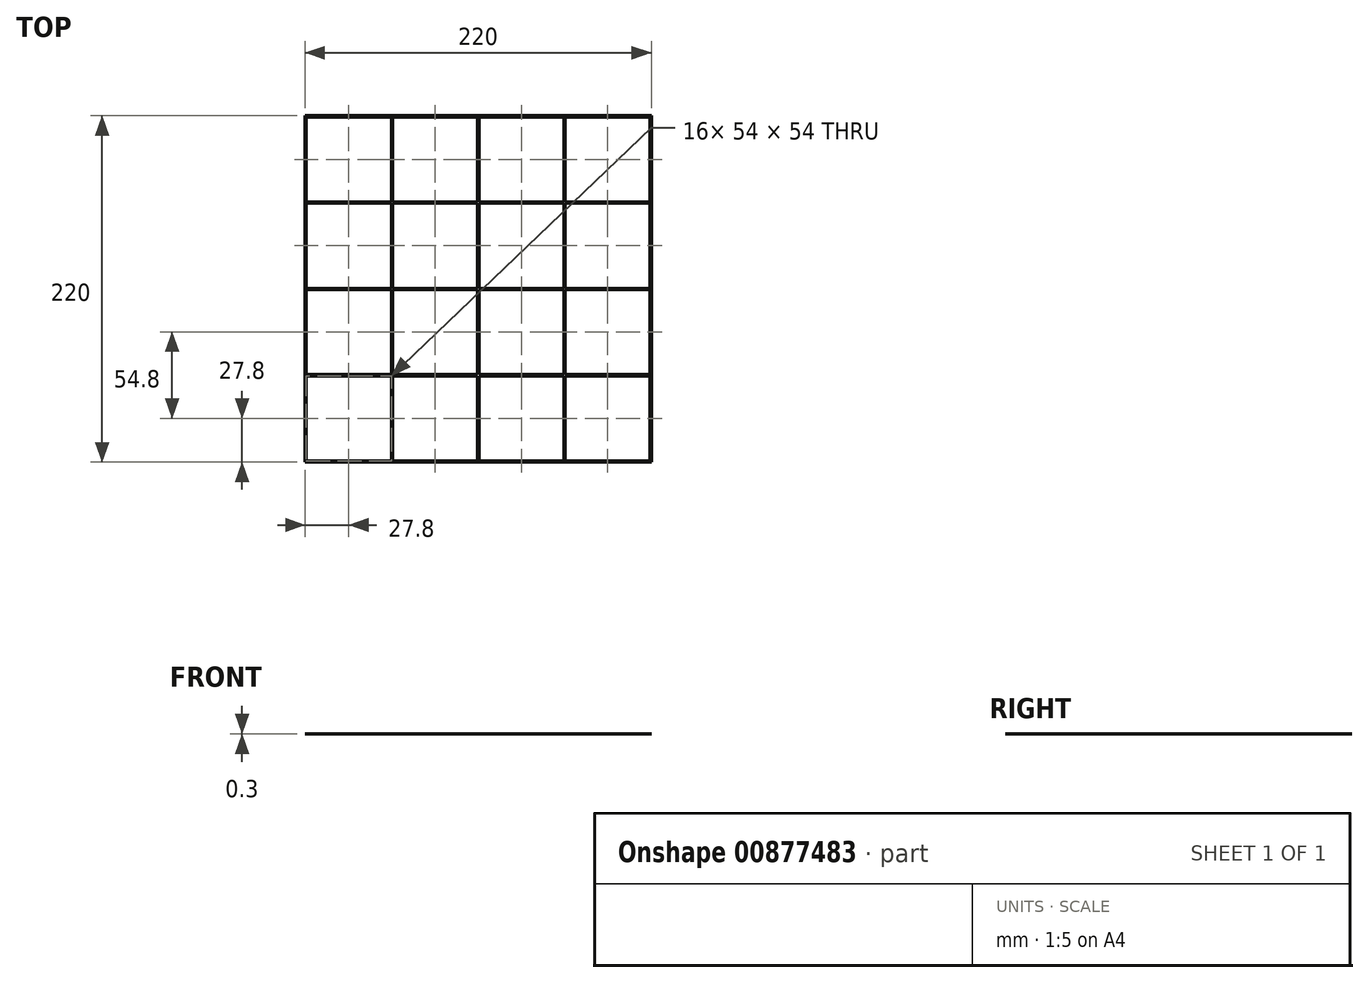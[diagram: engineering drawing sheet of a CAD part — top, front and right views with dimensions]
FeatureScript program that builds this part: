
annotation { "Feature Type Name" : "Feature", "Feature Type Description" : "" }
export const myFeature = defineFeature(function(context is Context, id is Id, definition is map)
    precondition{}
    {
        {
            var Q0;
            Q0=qCreatedBy(makeId("Top.planeOp"),FACE);
            var sketch = newSketch(context, id + "F0", { "sketchPlane" : qUnion([Q0])});
            skLineSegment(sketch, "E0.bottom", {"start": v(130, -130) * mm, "end": v(-130, -130) * mm, "construction": true});
            skLineSegment(sketch, "E0.top", {"start": v(130, 130) * mm, "end": v(-130, 130) * mm, "construction": true});
            skLineSegment(sketch, "E0.left", {"start": v(130, -130) * mm, "end": v(130, 130) * mm, "construction": true});
            skLineSegment(sketch, "E0.right", {"start": v(-130, -130) * mm, "end": v(-130, 130) * mm, "construction": true});
            skPoint(sketch, "E0.middle", {"position": v(0, 0) * mm});
            skLineSegment(sketch, "E1.0", {"start": v(-110, -110) * mm, "end": v(-110, 110) * mm});
            skLineSegment(sketch, "E1.1", {"start": v(110, -110) * mm, "end": v(-110, -110) * mm});
            skLineSegment(sketch, "E1.2", {"start": v(110, -110) * mm, "end": v(110, 110) * mm});
            skLineSegment(sketch, "E1.3", {"start": v(110, 110) * mm, "end": v(-110, 110) * mm});
            skLineSegment(sketch, "E2.0", {"start": v(-109.2, -109.2) * mm, "end": v(-109.2, -55.2) * mm, "construction": true});
            skLineSegment(sketch, "E2.1", {"start": v(109.2, -109.2) * mm, "end": v(55.2, -109.2) * mm, "construction": true});
            skLineSegment(sketch, "E2.2", {"start": v(109.2, -109.2) * mm, "end": v(109.2, -55.2) * mm, "construction": true});
            skLineSegment(sketch, "E2.3", {"start": v(109.2, 109.2) * mm, "end": v(55.2, 109.2) * mm, "construction": true});
            skLineSegment(sketch, "E3.bottom", {"start": v(-109.2, 109.2) * mm, "end": v(-55.2, 109.2) * mm});
            skLineSegment(sketch, "E3.top", {"start": v(-109.2, 0.4) * mm, "end": v(-55.2, 0.4) * mm});
            skLineSegment(sketch, "E3.left", {"start": v(-109.2, 109.2) * mm, "end": v(-109.2, 55.2) * mm});
            skLineSegment(sketch, "E3.right", {"start": v(-0.4, 109.2) * mm, "end": v(-0.4, 55.2) * mm});
            skLineSegment(sketch, "E4.MirrorCS", {"start": v(0.4, 109.2) * mm, "end": v(0.4, 55.2) * mm});
            skLineSegment(sketch, "E5.MirrorCS", {"start": v(109.2, 109.2) * mm, "end": v(55.2, 109.2) * mm});
            skLineSegment(sketch, "E6.MirrorCS", {"start": v(109.2, 0.4) * mm, "end": v(55.2, 0.4) * mm});
            skLineSegment(sketch, "E7.MirrorCS", {"start": v(109.2, 109.2) * mm, "end": v(109.2, 55.2) * mm});
            skLineSegment(sketch, "E8.MirrorCS", {"start": v(109.2, -109.2) * mm, "end": v(109.2, -55.2) * mm});
            skLineSegment(sketch, "E9.MirrorCS", {"start": v(109.2, -109.2) * mm, "end": v(55.2, -109.2) * mm});
            skLineSegment(sketch, "E10.MirrorCS", {"start": v(109.2, -0.4) * mm, "end": v(55.2, -0.4) * mm});
            skLineSegment(sketch, "E11.MirrorCS", {"start": v(0.4, -109.2) * mm, "end": v(0.4, -55.2) * mm});
            skLineSegment(sketch, "E12.MirrorCS", {"start": v(-0.4, -109.2) * mm, "end": v(-0.4, -55.2) * mm});
            skLineSegment(sketch, "E13.MirrorCS", {"start": v(-109.2, -109.2) * mm, "end": v(-55.2, -109.2) * mm});
            skLineSegment(sketch, "E14.MirrorCS", {"start": v(-109.2, -0.4) * mm, "end": v(-55.2, -0.4) * mm});
            skLineSegment(sketch, "E15.MirrorCS", {"start": v(-109.2, -109.2) * mm, "end": v(-109.2, -55.2) * mm});
            skPoint(sketch, "E16", {"position": v(-54.8, 109.2) * mm});
            skPoint(sketch, "E17", {"position": v(54.8, 109.2) * mm});
            skLineSegment(sketch, "E18", {"start": v(-55.2, 109.2) * mm, "end": v(-55.2, 55.2) * mm});
            skLineSegment(sketch, "E19", {"start": v(-54.4, 109.2) * mm, "end": v(-54.4, 55.2) * mm});
            skLineSegment(sketch, "E20.MirrorCS", {"start": v(54.4, 109.2) * mm, "end": v(54.4, 55.2) * mm});
            skLineSegment(sketch, "E21.MirrorCS", {"start": v(55.2, 109.2) * mm, "end": v(55.2, 55.2) * mm});
            skPoint(sketch, "E22", {"position": v(-109.2, 54.8) * mm});
            skLineSegment(sketch, "E23", {"start": v(-109.2, 55.2) * mm, "end": v(-55.2, 55.2) * mm});
            skLineSegment(sketch, "E24", {"start": v(-109.2, 54.4) * mm, "end": v(-55.2, 54.4) * mm});
            skLineSegment(sketch, "E25.MirrorCS", {"start": v(-109.2, -55.2) * mm, "end": v(-55.2, -55.2) * mm});
            skLineSegment(sketch, "E26.MirrorCS", {"start": v(-109.2, -54.4) * mm, "end": v(-55.2, -54.4) * mm});
            skLineSegment(sketch, "E27.trimOffspring", {"start": v(-54.4, 55.2) * mm, "end": v(-0.4, 55.2) * mm});
            skLineSegment(sketch, "E28.trimOffspring", {"start": v(-55.2, 54.4) * mm, "end": v(-55.2, 0.4) * mm});
            skLineSegment(sketch, "E29.trimOffspring", {"start": v(-54.4, 54.4) * mm, "end": v(-54.4, 0.4) * mm});
            skLineSegment(sketch, "E30.trimOffspring", {"start": v(-54.4, 54.4) * mm, "end": v(-0.4, 54.4) * mm});
            skLineSegment(sketch, "E31.trimOffspring", {"start": v(0.4, 55.2) * mm, "end": v(54.4, 55.2) * mm});
            skLineSegment(sketch, "E32.trimOffspring", {"start": v(-0.4, 54.4) * mm, "end": v(-0.4, 0.4) * mm});
            skLineSegment(sketch, "E33.trimOffspring", {"start": v(0.4, 54.4) * mm, "end": v(0.4, 0.4) * mm});
            skLineSegment(sketch, "E34.trimOffspring", {"start": v(0.4, 54.4) * mm, "end": v(54.4, 54.4) * mm});
            skLineSegment(sketch, "E35.trimOffspring", {"start": v(55.2, 55.2) * mm, "end": v(109.2, 55.2) * mm});
            skLineSegment(sketch, "E36.trimOffspring", {"start": v(55.2, 54.4) * mm, "end": v(109.2, 54.4) * mm});
            skLineSegment(sketch, "E37.trimOffspring", {"start": v(55.2, 54.4) * mm, "end": v(55.2, 0.4) * mm});
            skLineSegment(sketch, "E38.trimOffspring", {"start": v(54.4, 54.4) * mm, "end": v(54.4, 0.4) * mm});
            skLineSegment(sketch, "E39.trimOffspring", {"start": v(109.2, 55.2) * mm, "end": v(109.2, 109.2) * mm, "construction": true});
            skLineSegment(sketch, "E40.trimOffspring", {"start": v(54.4, 109.2) * mm, "end": v(0.4, 109.2) * mm, "construction": true});
            skLineSegment(sketch, "E41.trimOffspring", {"start": v(54.4, 109.2) * mm, "end": v(0.4, 109.2) * mm});
            skLineSegment(sketch, "E42.trimOffspring", {"start": v(-0.4, 109.2) * mm, "end": v(-54.4, 109.2) * mm, "construction": true});
            skLineSegment(sketch, "E43.trimOffspring", {"start": v(-55.2, 109.2) * mm, "end": v(-109.2, 109.2) * mm, "construction": true});
            skLineSegment(sketch, "E44.trimOffspring", {"start": v(-54.4, 109.2) * mm, "end": v(-0.4, 109.2) * mm});
            skLineSegment(sketch, "E45.trimOffspring", {"start": v(-109.2, 55.2) * mm, "end": v(-109.2, 109.2) * mm, "construction": true});
            skLineSegment(sketch, "E46.trimOffspring", {"start": v(-109.2, -0.4) * mm, "end": v(-109.2, 0.4) * mm, "construction": true});
            skLineSegment(sketch, "E47.trimOffspring", {"start": v(-55.2, -0.4) * mm, "end": v(-55.2, -54.4) * mm});
            skLineSegment(sketch, "E48.trimOffspring", {"start": v(-54.4, -0.4) * mm, "end": v(-54.4, -54.4) * mm});
            skLineSegment(sketch, "E49.trimOffspring", {"start": v(-54.4, 0.4) * mm, "end": v(-0.4, 0.4) * mm});
            skLineSegment(sketch, "E50.trimOffspring", {"start": v(-54.4, -0.4) * mm, "end": v(-0.4, -0.4) * mm});
            skLineSegment(sketch, "E51.trimOffspring", {"start": v(54.4, 0.4) * mm, "end": v(0.4, 0.4) * mm});
            skLineSegment(sketch, "E52.trimOffspring", {"start": v(54.4, -0.4) * mm, "end": v(54.4, -54.4) * mm});
            skLineSegment(sketch, "E53.trimOffspring", {"start": v(55.2, -0.4) * mm, "end": v(55.2, -54.4) * mm});
            skLineSegment(sketch, "E54.trimOffspring", {"start": v(54.4, -0.4) * mm, "end": v(0.4, -0.4) * mm});
            skLineSegment(sketch, "E55.trimOffspring", {"start": v(55.2, -54.4) * mm, "end": v(109.2, -54.4) * mm});
            skLineSegment(sketch, "E56.trimOffspring", {"start": v(54.4, -55.2) * mm, "end": v(54.4, -109.2) * mm});
            skLineSegment(sketch, "E57.trimOffspring", {"start": v(55.2, -55.2) * mm, "end": v(55.2, -109.2) * mm});
            skLineSegment(sketch, "E58.trimOffspring", {"start": v(109.2, -54.4) * mm, "end": v(109.2, -0.4) * mm, "construction": true});
            skLineSegment(sketch, "E59.trimOffspring", {"start": v(109.2, -54.4) * mm, "end": v(109.2, -0.4) * mm});
            skLineSegment(sketch, "E60.trimOffspring", {"start": v(54.4, -109.2) * mm, "end": v(0.4, -109.2) * mm, "construction": true});
            skLineSegment(sketch, "E61.trimOffspring", {"start": v(54.4, -109.2) * mm, "end": v(0.4, -109.2) * mm});
            skLineSegment(sketch, "E62.trimOffspring", {"start": v(-0.4, -109.2) * mm, "end": v(-54.4, -109.2) * mm, "construction": true});
            skLineSegment(sketch, "E63.trimOffspring", {"start": v(-55.2, -109.2) * mm, "end": v(-109.2, -109.2) * mm, "construction": true});
            skLineSegment(sketch, "E64.trimOffspring", {"start": v(-54.4, -109.2) * mm, "end": v(-0.4, -109.2) * mm});
            skLineSegment(sketch, "E65.trimOffspring", {"start": v(-54.4, -54.4) * mm, "end": v(-0.4, -54.4) * mm});
            skLineSegment(sketch, "E66.trimOffspring", {"start": v(-55.2, -55.2) * mm, "end": v(-55.2, -109.2) * mm});
            skLineSegment(sketch, "E67.trimOffspring", {"start": v(-54.4, -55.2) * mm, "end": v(-54.4, -109.2) * mm});
            skLineSegment(sketch, "E68.trimOffspring", {"start": v(-54.4, -55.2) * mm, "end": v(-0.4, -55.2) * mm});
            skLineSegment(sketch, "E69.trimOffspring", {"start": v(0.4, -54.4) * mm, "end": v(54.4, -54.4) * mm});
            skLineSegment(sketch, "E70.trimOffspring", {"start": v(0.4, -54.4) * mm, "end": v(0.4, -0.4) * mm});
            skLineSegment(sketch, "E71.trimOffspring", {"start": v(-0.4, -54.4) * mm, "end": v(-0.4, -0.4) * mm});
            skLineSegment(sketch, "E72.trimOffspring", {"start": v(0.4, -55.2) * mm, "end": v(109.2, -55.2) * mm});
            skLineSegment(sketch, "E73", {"start": v(-109.2, 54.4) * mm, "end": v(-109.2, 0.4) * mm});
            skLineSegment(sketch, "E74.trimOffspring", {"start": v(109.2, 54.4) * mm, "end": v(109.2, 0.4) * mm});
            skLineSegment(sketch, "E75.trimOffspring", {"start": v(109.2, 0.4) * mm, "end": v(109.2, 54.4) * mm, "construction": true});
            skLineSegment(sketch, "E76", {"start": v(-109.2, -54.4) * mm, "end": v(-109.2, -0.4) * mm});
            skSolve(sketch);
        }
        {
            var Q0;
            Q0=makeQuery(id+"F0.imprint","IMPRINT",FACE,{"disambiguationData":[TD([[makeQuery(id+"F0.imprint","IMPRINT",EDGE,{"derivedFrom":sQuery(id+"F0.wireOp",EDGE,"E1.0")}),-1.0]])]});
            extrude(context, id + "F1", {"entities" : qUnion([Q0]), "flatOperationType" : FlatOperationType.REMOVE, "oppositeDirection" : true, "depth" : .3 * mm, "offsetDistance" : 25 * mm, "domain" : OperationDomain.MODEL});
        }
    });
